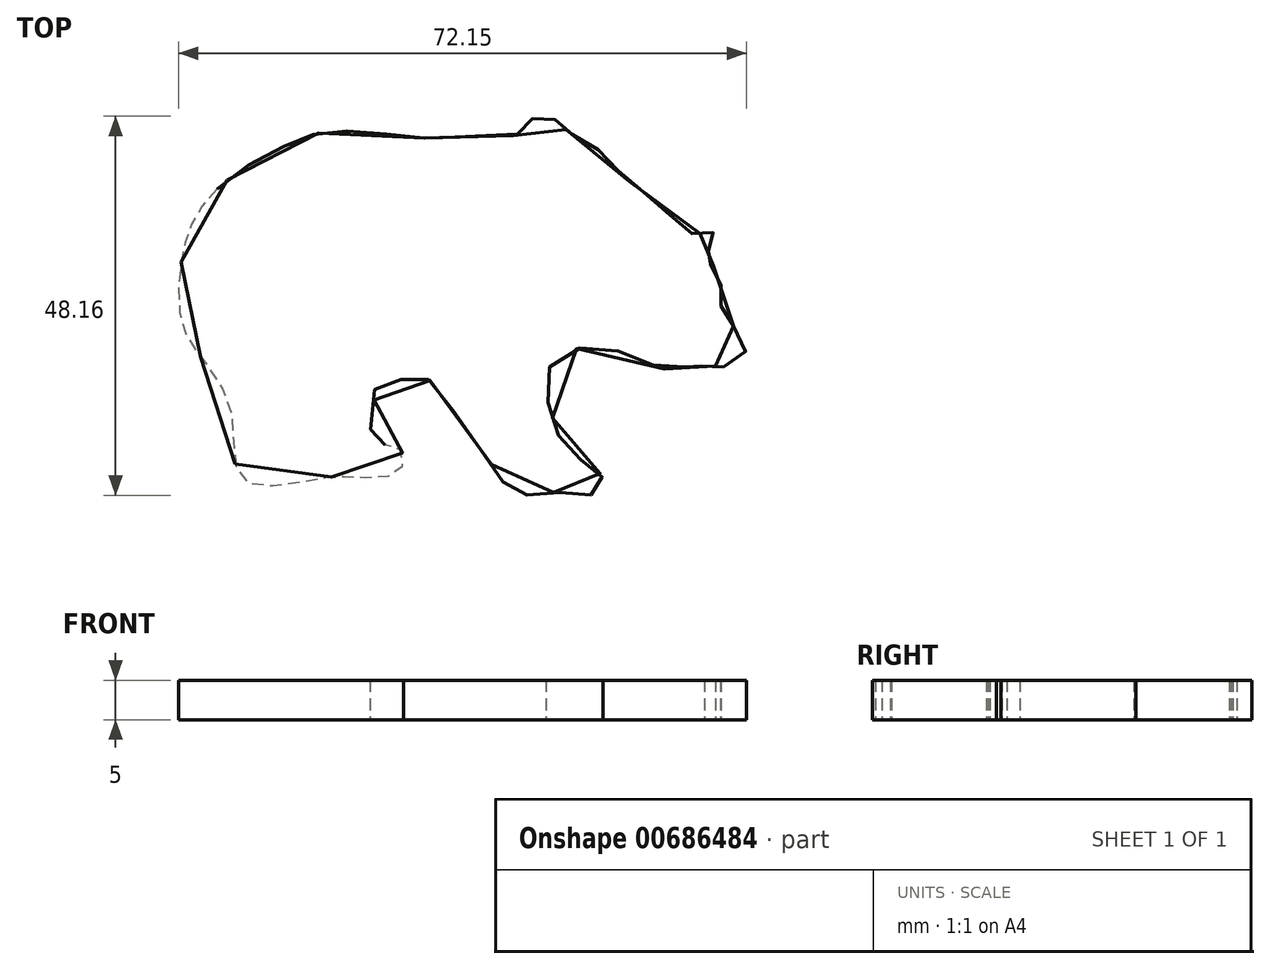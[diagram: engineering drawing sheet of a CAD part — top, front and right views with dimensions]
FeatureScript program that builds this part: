
annotation { "Feature Type Name" : "Feature", "Feature Type Description" : "" }
export const myFeature = defineFeature(function(context is Context, id is Id, definition is map)
    precondition{}
    {
        {
            var Q0;
            Q0=qCreatedBy(makeId("Top.planeOp"),FACE);
            var sketch = newSketch(context, id + "F0", { "sketchPlane" : qUnion([Q0])});
            skPoint(sketch, "E0.1.internal.snap0", {"position": v(0, 23.8) * mm});
            skFitSpline(sketch, "E0", {"points": [v(-1.66, 21.3) * mm, v(-3.22, 23.8) * mm, v(-3.22, 25.8) * mm, v(-4.2, 28.92) * mm, v(-5.37, 29.7) * mm, v(-4, 32.24) * mm, v(-4.4, 33.22) * mm, v(-6.94, 33.02) * mm, v(-10.45, 36.15) * mm, v(-15.53, 40.25) * mm, v(-18.66, 43.57) * mm, v(-22.57, 45.92) * mm, v(-24.52, 47.6) * mm, v(-27.26, 47.6) * mm, v(-29.01, 45.72) * mm, v(-34.3, 45.52) * mm, v(-38.98, 45.13) * mm, v(-46.01, 45.72) * mm, v(-53.63, 45.92) * mm, v(-58.71, 44.16) * mm, v(-65.94, 39.86) * mm, v(-70.24, 34.78) * mm, v(-71.8, 29.5) * mm, v(-71.8, 21.88) * mm, v(-69.07, 17) * mm, v(-65.36, 9.77) * mm, v(-63.99, 1.76) * mm, v(-55.2, 1.76) * mm, v(-49.92, 2.15) * mm, v(-44.06, 2.93) * mm, v(-44.25, 5.86) * mm, v(-47.58, 6.45) * mm, v(-47.38, 10.16) * mm, v(-46.6, 14.46) * mm, v(-41.71, 14.26) * mm, v(-40.35, 14.46) * mm, v(-36.24, 8.99) * mm, v(-32.14, 3.32) * mm, v(-29.4, 0) * mm, v(-26.47, 0) * mm, v(-22.18, 0) * mm, v(-19.25, 0) * mm, v(-18.27, 1.76) * mm, v(-19.44, 3.32) * mm, v(-22.76, 5.67) * mm, v(-24.52, 9.18) * mm, v(-25.5, 13.87) * mm, v(-23.54, 17.78) * mm, v(-17.68, 18.37) * mm, v(-13.77, 17.2) * mm, v(-8.3, 15.63) * mm, v(-7.33, 16.8) * mm, v(-5.76, 16.22) * mm, v(-4, 16.22) * mm, v(-2.05, 16.22) * mm, v(0, 18.56) * mm, v(-1.66, 21.3) * mm]});
            skSolve(sketch);
        }
        {
            var Q0;
            Q0 = qSketchRegion(id + "F0", true);
            extrude(context, id + "F1", {"entities" : qUnion([Q0]), "depth" : 5 * mm, "offsetDistance" : 25.4 * mm});
        }
    });
